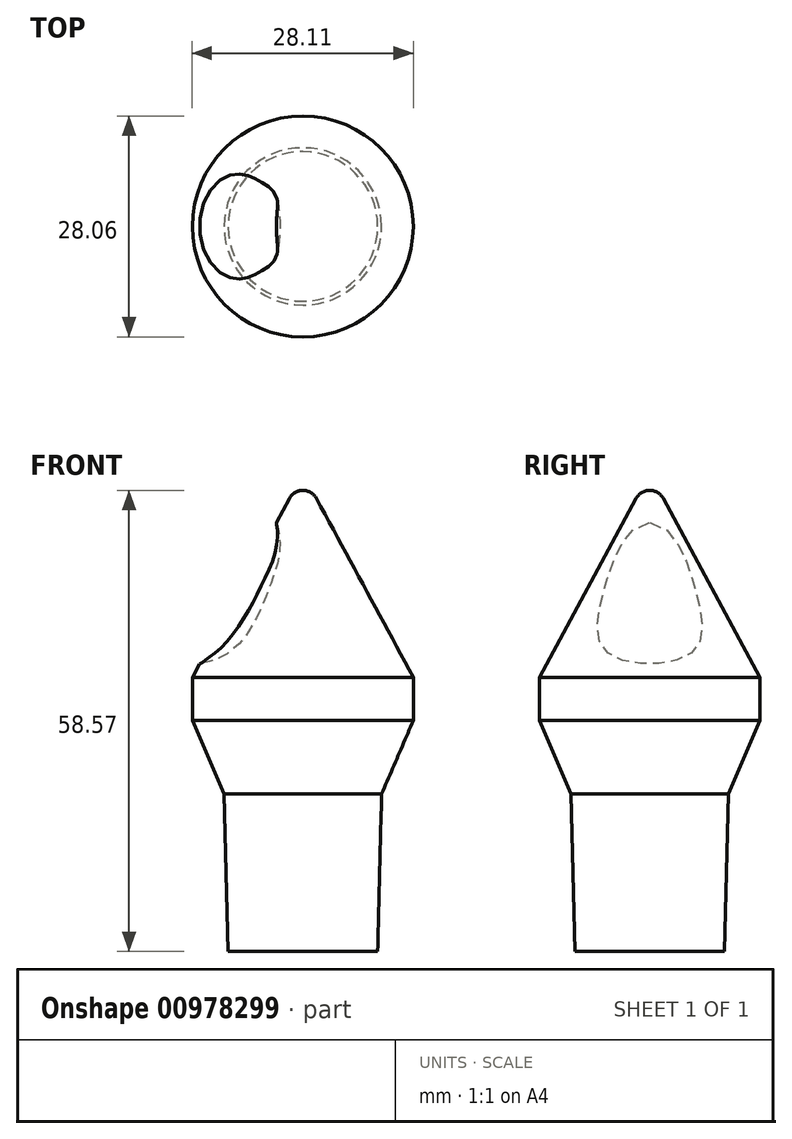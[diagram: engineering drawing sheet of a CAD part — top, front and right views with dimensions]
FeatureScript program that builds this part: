
annotation { "Feature Type Name" : "Feature", "Feature Type Description" : "" }
export const myFeature = defineFeature(function(context is Context, id is Id, definition is map)
    precondition{}
    {
        {
            var Q0;
            Q0=qCreatedBy(makeId("Front.planeOp"),FACE);
            var sketch = newSketch(context, id + "F0", { "sketchPlane" : qUnion([Q0])});
            skLineSegment(sketch, "E0", {"start": v(0, 0) * mm, "end": v(0, -20) * mm});
            skLineSegment(sketch, "E1", {"start": v(0, -20) * mm, "end": v(-9.5, -20) * mm});
            skLineSegment(sketch, "E2", {"start": v(-9.5, -20) * mm, "end": v(-10, 0) * mm});
            skLineSegment(sketch, "E3", {"start": v(-10, 0) * mm, "end": v(-14.03, 9.35) * mm});
            skLineSegment(sketch, "E4", {"start": v(-14.03, 9.35) * mm, "end": v(-14.03, 14.82) * mm});
            skLineSegment(sketch, "E5", {"start": v(-14.03, 14.82) * mm, "end": v(-1.72, 37.54) * mm});
            skLineSegment(sketch, "E6", {"start": v(0, 38.57) * mm, "end": v(0, 0) * mm});
            skArc(sketch, "E7", {"start": v(0, 38.57) * mm, "mid": v(-1, 38.3) * mm, "end": v(-1.72, 37.54) * mm});
            skSolve(sketch);
        }
        {
            var Q0;
            Q0=makeQuery(id+"F0.imprint","IMPRINT",FACE,{"disambiguationData":[TD([[makeQuery(id+"F0.imprint","IMPRINT",EDGE,{"derivedFrom":sQuery(id+"F0.wireOp",EDGE,"E0")}),-1.0]])]});
            var Q1;
            Q1=sQuery(id+"F0.wireOp",EDGE,"E6");
            revolve(context, id + "F1", {"surfaceOperationType" : NewSurfaceOperationType.NEW, "entities" : qUnion([Q0]), "axis" : qUnion([Q1]), "revolveType" : RevolveType.FULL});
        }
        {
            var Q0;
            Q0=qCreatedBy(makeId("Front.planeOp"),FACE);
            var sketch = newSketch(context, id + "F2", { "sketchPlane" : qUnion([Q0])});
            skLineSegment(sketch, "E8", {"start": v(-11.74, 45.18) * mm, "end": v(-27.66, 17.42) * mm});
            skFitSpline(sketch, "E9", {"points": [v(-27.66, 17.42) * mm, v(-10.34, 17.42) * mm, v(-4.4, 25.92) * mm, v(-3.26, 34.13) * mm, v(-11.74, 45.18) * mm], "startDerivative": vector(60.1, -9.01) * mm, "endDerivative": vector(-36.94, 27.96) * mm});
            skSolve(sketch);
        }
        {
            var Q0;
            Q0=makeQuery(id+"F2.imprint","IMPRINT",FACE,{"disambiguationData":[TD([[makeQuery(id+"F2.imprint","IMPRINT",EDGE,{"derivedFrom":sQuery(id+"F2.wireOp",EDGE,"E8")}),1.0]])]});
            var Q1;
            Q1=sQuery(id+"F2.wireOp",EDGE,"E8");
            revolve(context, id + "F3", {"surfaceOperationType" : NewSurfaceOperationType.NEW, "entities" : qUnion([Q0]), "axis" : qUnion([Q1]), "revolveType" : RevolveType.FULL});
        }
        {
            var Q0;
            Q0=makeQuery(id+"F3.opRevolve","SWEPT_BODY",BODY,{"disambiguationData":[OSD([sQuery(id+"F2.wireOp",EDGE,"E8"),sQuery(id+"F2.wireOp",EDGE,"E9")])]});
            var Q1;
            Q1=makeQuery(id+"FeKX7c5hyGLTON1_1.2.F3.opRevolve","SWEPT_BODY",BODY,{"disambiguationData":[OSD([sQuery(id+"F2.wireOp",EDGE,"E8"),sQuery(id+"F2.wireOp",EDGE,"E9")])]});
            var Q2;
            Q2=makeQuery(id+"FeKX7c5hyGLTON1_1.1.F3.opRevolve","SWEPT_BODY",BODY,{"disambiguationData":[OSD([sQuery(id+"F2.wireOp",EDGE,"E8"),sQuery(id+"F2.wireOp",EDGE,"E9")])]});
            var Q3;
            Q3=makeQuery(id+"F1.opRevolve","SWEPT_BODY",BODY,{"disambiguationData":[OSD([sQuery(id+"F0.wireOp",EDGE,"E0"),sQuery(id+"F0.wireOp",EDGE,"E1"),sQuery(id+"F0.wireOp",EDGE,"E2"),sQuery(id+"F0.wireOp",EDGE,"E3"),sQuery(id+"F0.wireOp",EDGE,"E4"),sQuery(id+"F0.wireOp",EDGE,"E5"),sQuery(id+"F0.wireOp",EDGE,"E6"),sQuery(id+"F0.wireOp",EDGE,"E7")])]});
            booleanBodies(context, id + "F4", {"operationType" : BooleanOperationType.SUBTRACTION, "tools" : qUnion([Q0, Q1, Q2]), "targets" : qUnion([Q3])});
        }
    });
